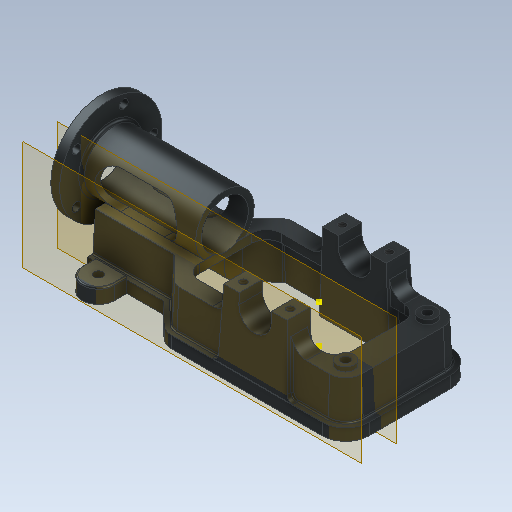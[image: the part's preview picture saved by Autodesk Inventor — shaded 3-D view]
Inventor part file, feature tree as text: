
AUTODESK INVENTOR PART (.ipt)
format: ipt  version: 2020 (Build 240168000, 168)  size: 751,616 bytes
history: native  units: mm
features: sketch x19, extrude x16, draft x9, projected_geometry x6, fillet x5, thread x4, plane x2, boolean_combine x2, hole x1
ambient origin geometry x8: Origin, YZ Plane, XZ Plane, XY Plane, X Axis, Y Axis, Z Axis, Center Point
bodies: Solid1 (feature_tree), Solid2 (feature_tree), Solid3 (feature_tree)
feature tree (64):
  extrude  "Extrusion1"  Depth=44.0mm
  extrude  "Extrusion2"  Depth=26.0mm
  fillet  "Fillet1"  Radius=26.5mm
  sketch  "Sketch3"  dims[d5=9.0mm d6=6.0mm]
  extrude  "Extrusion3"  Depth=6.0mm
  draft  "FaceDraft1"
  draft  "FaceDraft2"
  extrude  "Extrusion4"  Depth=5.0mm
  draft  "FaceDraft3"
  draft  "FaceDraft4"
  draft  "FaceDraft5"
  sketch  "Sketch7"  dims[d11=6.0mm d12=4.0mm d13=0.0mm]
  sketch  "Sketch8"  dims[d14=11.0mm d15=17.5mm]
  extrude  "Extrusion6"  Depth=3.0mm
  extrude  "Extrusion7"  Depth=4.0mm TaperAngle=0.0deg
  extrude  "Extrusion8"  Depth=17.5mm
  plane  "Work Plane1"
  extrude  "Extrusion9"  Depth=17.5mm
  extrude  "Extrusion10"  Depth=8.0mm
  extrude  "Extrusion11"  Depth=3.0mm
  fillet  "Fillet2"  Radius=3.0mm
  extrude  "Extrusion12"  Depth=0.5mm
  extrude  "Extrusion13"  Depth=0.436332mm
  extrude  "Extrusion14"  TaperAngle=0.0deg  [1 undecoded]
  extrude  "Extrusion15"  Depth=0.436332mm
  draft  "FaceDraft9"
  draft  "FaceDraft10"
  draft  "FaceDraft11"
  plane  "Work Plane2"
  extrude  "Extrusion16"  Depth=0.436332mm
  boolean_combine  "Combine1"
  extrude  "Extrusion17"  Depth=52.0mm
  draft  "FaceDraft12"
  sketch  "Sketch20"  dims[d55=25.0mm d56=0.0mm d57=35.0mm d58=3.0mm d59=0.0mm d60=16.0mm d61=3.0mm d62=0.0mm d63=1.0mm d64=3.0mm d65=14.5mm d66=50.0mm d68=360.0deg d70=3.0mm d71=0.0mm d72=3.0mm d73=3.0mm d74=14.0mm d75=89.0mm d76=14.0mm d77=89.0mm d78=3.0mm d79=0.0mm d80=6.0mm d81=6.0mm d82=1.5mm d83=0.0mm d84=24.0mm d85=27.0mm d86=0.0mm d87=31.25mm d88=9.0mm d89=0.0mm d93=0.436332mm d94=0.436332mm d95=-0.436332mm d96=11.75mm d97=11.0mm d98=3.5mm d99=10.820031mm d100=10.820031mm d101=9.0mm d102=0.0mm d103=9.0mm d104=0.0mm d105=0.436332mm d106=3.9105mm d107=3.910655mm d108=3.911mm d109=16.0mm d110=2.82mm d111=2.820063mm d112=3.911mm d113=3.911mm d114=2.5mm d115=6.0mm d116=6.0mm d117=2.0mm d118=90.0deg d119=7.0mm d120=20.594885mm d121=10.0mm d122=0.0mm d123=10.0mm d124=0.0mm d125=10.0mm d126=0.0mm d127=10.0mm d128=0.0mm d129=16.0mm d130=2.82mm d131=5.0mm d132=2.0mm d133=0.5mm]
  boolean_combine  "Combine2"
  hole  "Hole1"  [1 undecoded]
  thread  "Thread1"  [1 undecoded]
  thread  "Thread2"  [1 undecoded]
  thread  "Thread3"  [1 undecoded]
  thread  "Thread4"  [1 undecoded]
  fillet  "Fillet3"  Radius=15.0mm
  fillet  "Fillet4"  Radius=13.0mm
  fillet  "Fillet5"  Radius=13.0mm
  sketch  "Sketch1"  dims[d0=62.0mm d1=44.0mm]
  sketch  "Sketch2"  dims[d2=8.0mm d3=26.0mm d4=26.5mm]
  sketch  "Sketch4"  dims[d7=5.0mm d8=5.0mm]
  projected_geometry  "Projected Loop1"
  sketch  "Sketch5"  dims[d9=5.0mm d10=3.0mm]
  projected_geometry  "Projected Loop3"
  sketch  "Sketch9"  dims[d16=11.0mm d17=17.5mm]
  sketch  "Sketch10"  dims[d18=35.0mm d19=8.0mm]
  sketch  "Sketch11"  dims[d20=8.0mm d21=3.0mm d22=3.0mm]
  projected_geometry  "Projected Loop4"
  sketch  "Sketch12"  dims[d23=5.0mm d24=0.0mm d25=0.5mm]
  sketch  "Sketch13"  dims[d26=13.0mm d27=0.0mm d28=0.436332mm]
  sketch  "Sketch14"  dims[d29=0.436332mm d30=0.0mm]
  projected_geometry  "Projected Loop5"
  sketch  "Sketch15"  dims[d31=13.0mm d32=0.0mm d33=0.436332mm]
  sketch  "Sketch16"  dims[d34=0.436332mm d37=0.436332mm]
  sketch  "Sketch17"  dims[d38=3.0mm d39=0.0mm d40=52.0mm]
  sketch  "Sketch18"  dims[d41=28.0mm d42=11.0mm d43=5.0mm d44=0.0mm d45=0.0mm d46=20.0mm d47=24.0mm]
  projected_geometry  "Projected Loop6"
  sketch  "Sketch19"  dims[d48=8.25mm d49=33.75mm d50=0.0mm d51=0.0mm d52=15.0mm d53=13.0mm d54=13.0mm]
  projected_geometry  "Projected Loop7"
note: 6 required parameter values undecoded (feature->parameter linkage not recoverable at this tier; creation-order binding heuristic only, values carry confidence <= 0.55)
